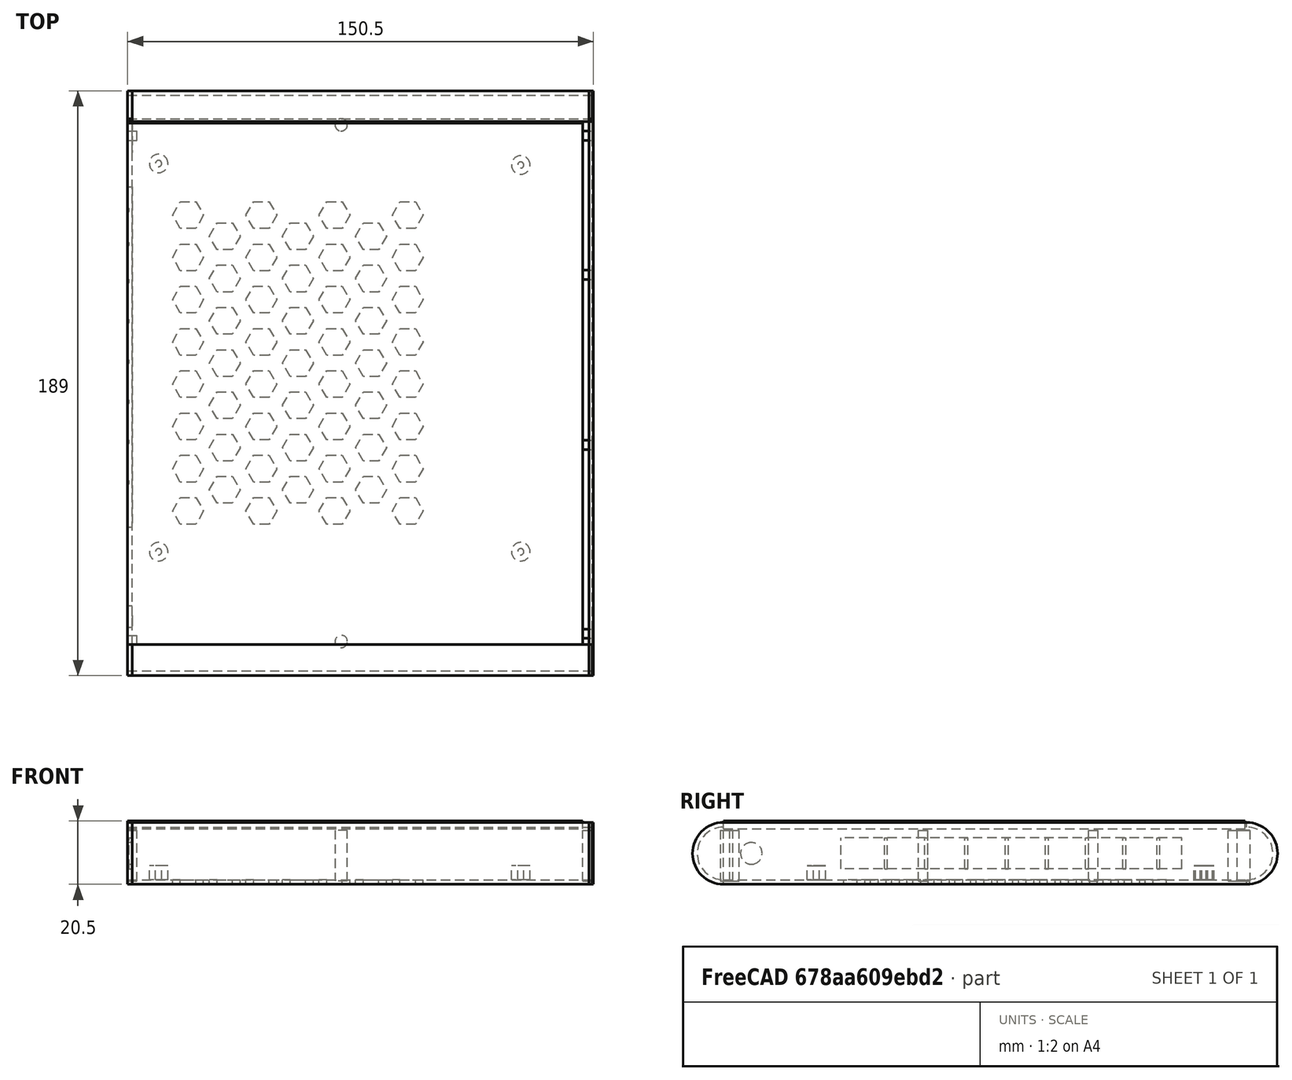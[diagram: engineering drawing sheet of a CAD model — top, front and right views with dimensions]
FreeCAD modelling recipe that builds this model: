
FCSTD DOCUMENT  (FreeCAD 0.20R29603 (Git))
Label: case1
License: All rights reserved
LicenseURL: http://en.wikipedia.org/wiki/All_rights_reserved
objects: Part::Box×20, Part::FeaturePython×7, Part::Cylinder×7, Part::MultiFuse×5, Part::Cut×4, App::DocumentObjectGroup×2
note: 43 computed .brp shape members not serialized (recipe doc carries the construction recipe); baked Part::Feature solids carry a one-line shape summary decoded from their .brp

FEATURE [Part::Box] Box  label="base"
  AttacherType = Attacher::AttachEngine3D
  Height = 1.5
  Length = 150
  Placement = pos=(0,0,-10) rot=(1,0,0;0rad)
  Width = 170
FEATURE [Part::FeaturePython] Tube  label="LeftCurve"  # WARN: FeaturePython — macro-defined, semantics opaque (R4)
  AttacherType = Attacher::AttachEngine3D
  Height = 150
  InnerRadius = 8.5
  OuterRadius = 10
  Placement = pos=(0,0,0) rot=(0,1,0;1.5708rad)
FEATURE [Part::FeaturePython] Tube001  label="RightCurve"  # WARN: FeaturePython — macro-defined, semantics opaque (R4)
  AttacherType = Attacher::AttachEngine3D
  Height = 150
  InnerRadius = 8.5
  OuterRadius = 10
  Placement = pos=(0,169,0) rot=(0,1,0;1.5708rad)
FEATURE [Part::Cylinder] Cylinder
  Angle = 360
  AttacherType = Attacher::AttachEngine3D
  FirstAngle = 0
  Height = 1.5
  Placement = pos=(0,0,0) rot=(0,1,0;1.5708rad)
  Radius = 10
  SecondAngle = 0
FEATURE [Part::Cylinder] Cylinder001
  Angle = 360
  AttacherType = Attacher::AttachEngine3D
  FirstAngle = 0
  Height = 1.5
  Placement = pos=(0,169,0) rot=(0,1,0;1.5708rad)
  Radius = 10
  SecondAngle = 0
FEATURE [Part::Box] Box001  label="Cube001"
  AttacherType = Attacher::AttachEngine3D
  Height = 20
  Length = 1.5
  Placement = pos=(0,0,-10) rot=(0,0,1;0rad)
  Width = 170
FEATURE [Part::MultiFuse] Fusion  label="Front"
  Placement = pos=(149,0,0) rot=(0,0,1;0rad)
  Shapes = -> [Cylinder,Cylinder001,Box001]
FEATURE [Part::Box] Box002  label="Cube002"
  AttacherType = Attacher::AttachEngine3D
  Height = 20
  Length = 1.5
  Placement = pos=(0,0,-10) rot=(0,0,1;0rad)
  Width = 170
FEATURE [Part::Cylinder] Cylinder002
  Angle = 360
  AttacherType = Attacher::AttachEngine3D
  FirstAngle = 0
  Height = 1.5
  Placement = pos=(0,0,0) rot=(0,1,0;1.5708rad)
  Radius = 10
  SecondAngle = 0
FEATURE [Part::Cylinder] Cylinder003
  Angle = 360
  AttacherType = Attacher::AttachEngine3D
  FirstAngle = 0
  Height = 1.5
  Placement = pos=(0,169,0) rot=(0,1,0;1.5708rad)
  Radius = 10
  SecondAngle = 0
FEATURE [Part::MultiFuse] Fusion001  label="back"
  Shapes = -> [Cylinder002,Cylinder003,Box002]
FEATURE [Part::MultiFuse] Fusion002  label="Sides"
  Shapes = -> [Tube,Tube001]
FEATURE [Part::Box] Box003  label="Cube"
  AttacherType = Attacher::AttachEngine3D
  Height = 22
  Length = 150
  Placement = pos=(0,0,-11) rot=(0,0,1;0rad)
  Width = 169
FEATURE [Part::Cut] Cut
  Base = -> Fusion002
  Tool = -> Box003
FEATURE [Part::FeaturePython] Tube002  # WARN: FeaturePython — macro-defined, semantics opaque (R4)
  AttacherType = Attacher::AttachEngine3D
  Height = 5
  InnerRadius = 1
  OuterRadius = 3
  Placement = pos=(10,10,-9) rot=(0,0,1;0rad)
FEATURE [Part::FeaturePython] Tube003  # WARN: FeaturePython — macro-defined, semantics opaque (R4)
  AttacherType = Attacher::AttachEngine3D
  Height = 5
  InnerRadius = 1
  OuterRadius = 3
  Placement = pos=(10,135.5,-9) rot=(0,0,1;0rad)
FEATURE [Part::FeaturePython] Tube004  # WARN: FeaturePython — macro-defined, semantics opaque (R4)
  AttacherType = Attacher::AttachEngine3D
  Height = 5
  InnerRadius = 1
  OuterRadius = 3
  Placement = pos=(127,135,-9) rot=(0,0,1;0rad)
FEATURE [Part::FeaturePython] Tube005  # WARN: FeaturePython — macro-defined, semantics opaque (R4)
  AttacherType = Attacher::AttachEngine3D
  Height = 5
  InnerRadius = 1
  OuterRadius = 3
  Placement = pos=(127,10,-9) rot=(0,0,1;0rad)
FEATURE [Part::Box] Box004  label="Cube003"
  AttacherType = Attacher::AttachEngine3D
  Height = 10
  Length = 10
  Placement = pos=(-3,38,-5) rot=(0,0,1;0rad)
  Width = 110
FEATURE [Part::Box] Box005  label="top"
  AttacherType = Attacher::AttachEngine3D
  Height = 2.5
  Length = 147
  Placement = pos=(0,0,8) rot=(1,0,0;0rad)
  Width = 168.5
FEATURE [Part::Cut] Cut001
  Base = -> Fusion001
  Tool = -> Box004
FEATURE [Part::MultiFuse] Fusion003
  Placement = pos=(0,20,0) rot=(0,0,1;0rad)
  Shapes = -> [Tube002,Tube003,Tube004,Tube005]
FEATURE [Part::FeaturePython] HoneycombSolid  # WARN: FeaturePython — macro-defined, semantics opaque (R4)
  Circumradius = 5
  Height = 2
  Length = 70
  Placement = pos=(20,51,-10) rot=(0,0,1;0rad)
  Thickness = 5
  UseContainer = false
  Width = 80
FEATURE [Part::Cut] Cut002
  Base = -> Box
  Tool = -> HoneycombSolid
FEATURE [Part::Cylinder] Cylinder004  label="pwrjack"
  Angle = 360
  AttacherType = Attacher::AttachEngine3D
  FirstAngle = 0
  Height = 10
  Placement = pos=(-3,9,0) rot=(0,1,0;1.5708rad)
  Radius = 3.5
  SecondAngle = 0
FEATURE [Part::Cut] Cut003
  Base = -> Cut001
  Tool = -> Cylinder004
FEATURE [Part::Box] Box006  label="Cube004"
  AttacherType = Attacher::AttachEngine3D
  Height = 16.5
  Length = 3
  Placement = pos=(0,0,-9) rot=(0,0,1;0rad)
  Width = 3
FEATURE [Part::Box] Box007  label="Cube005"
  AttacherType = Attacher::AttachEngine3D
  Height = 16.5
  Length = 3
  Placement = pos=(0,163,-9) rot=(0,0,1;0rad)
  Width = 3
FEATURE [Part::Box] Box008  label="Cube006"
  AttacherType = Attacher::AttachEngine3D
  Height = 16.5
  Length = 3
  Placement = pos=(147,118,-9) rot=(0,0,1;0rad)
  Width = 3
FEATURE [Part::Box] Box009  label="Cube007"
  AttacherType = Attacher::AttachEngine3D
  Height = 16.5
  Length = 3
  Placement = pos=(147,163,-9) rot=(0,0,1;0rad)
  Width = 3
FEATURE [Part::Box] Box010  label="Cube008"
  AttacherType = Attacher::AttachEngine3D
  Height = 16.5
  Length = 3
  Placement = pos=(147,63,-9) rot=(0,0,1;0rad)
  Width = 3
FEATURE [Part::Box] Box011  label="Cube009"
  AttacherType = Attacher::AttachEngine3D
  Height = 16.5
  Length = 3
  Placement = pos=(147,2,-9) rot=(0,0,1;0rad)
  Width = 3
FEATURE [Part::Cylinder] Cylinder005
  Angle = 360
  AttacherType = Attacher::AttachEngine3D
  FirstAngle = 0
  Height = 16.5
  Placement = pos=(69,1,-9) rot=(0,0,1;0rad)
  Radius = 2
  SecondAngle = 0
FEATURE [Part::Cylinder] Cylinder006
  Angle = 360
  AttacherType = Attacher::AttachEngine3D
  FirstAngle = 0
  Height = 16.5
  Placement = pos=(69,168,-9) rot=(0,0,1;0rad)
  Radius = 2
  SecondAngle = 0
FEATURE [App::DocumentObjectGroup] Group001  label="CaseTop"
  Group = -> [Box005]
FEATURE [Part::Box] Box012  label="Cube010"
  AttacherType = Attacher::AttachEngine3D
  Height = 10
  Length = 0.5
  Placement = pos=(0,65,-5) rot=(0,0,1;0rad)
  Width = 1
FEATURE [Part::Box] Box013  label="Cube011"
  AttacherType = Attacher::AttachEngine3D
  Height = 10
  Length = 0.5
  Placement = pos=(0,52,-5) rot=(0,0,1;0rad)
  Width = 1
FEATURE [Part::Box] Box014  label="Cube012"
  AttacherType = Attacher::AttachEngine3D
  Height = 10
  Length = 0.5
  Placement = pos=(0,78,-5) rot=(0,0,1;0rad)
  Width = 1
FEATURE [Part::Box] Box015  label="Cube013"
  AttacherType = Attacher::AttachEngine3D
  Height = 10
  Length = 0.5
  Placement = pos=(0,91,-5) rot=(0,0,1;0rad)
  Width = 1
FEATURE [Part::Box] Box016  label="Cube014"
  AttacherType = Attacher::AttachEngine3D
  Height = 10
  Length = 0.5
  Placement = pos=(0,104,-5) rot=(0,0,1;0rad)
  Width = 1
FEATURE [Part::Box] Box017  label="Cube015"
  AttacherType = Attacher::AttachEngine3D
  Height = 10
  Length = 0.5
  Placement = pos=(0,117,-5) rot=(0,0,1;0rad)
  Width = 1
FEATURE [Part::Box] Box018  label="Cube016"
  AttacherType = Attacher::AttachEngine3D
  Height = 10
  Length = 0.5
  Placement = pos=(0,129,-5) rot=(0,0,1;0rad)
  Width = 1
FEATURE [Part::Box] Box019  label="Cube017"
  AttacherType = Attacher::AttachEngine3D
  Height = 10
  Length = 0.5
  Placement = pos=(0,140,-5) rot=(0,0,1;0rad)
  Width = 1
FEATURE [Part::MultiFuse] Fusion004
  Shapes = -> [Fusion003,Cut002]
FEATURE [App::DocumentObjectGroup] Group  label="CaseBase"
  Group = -> [Fusion,Cut,Cut003,Box006,Box007,Box008,Box009,Box010,Box011,Cylinder005,Cylinder006,Box012,Box013,Box014,Box015,Box016,Box017,Box018,Box019,Fusion004]
